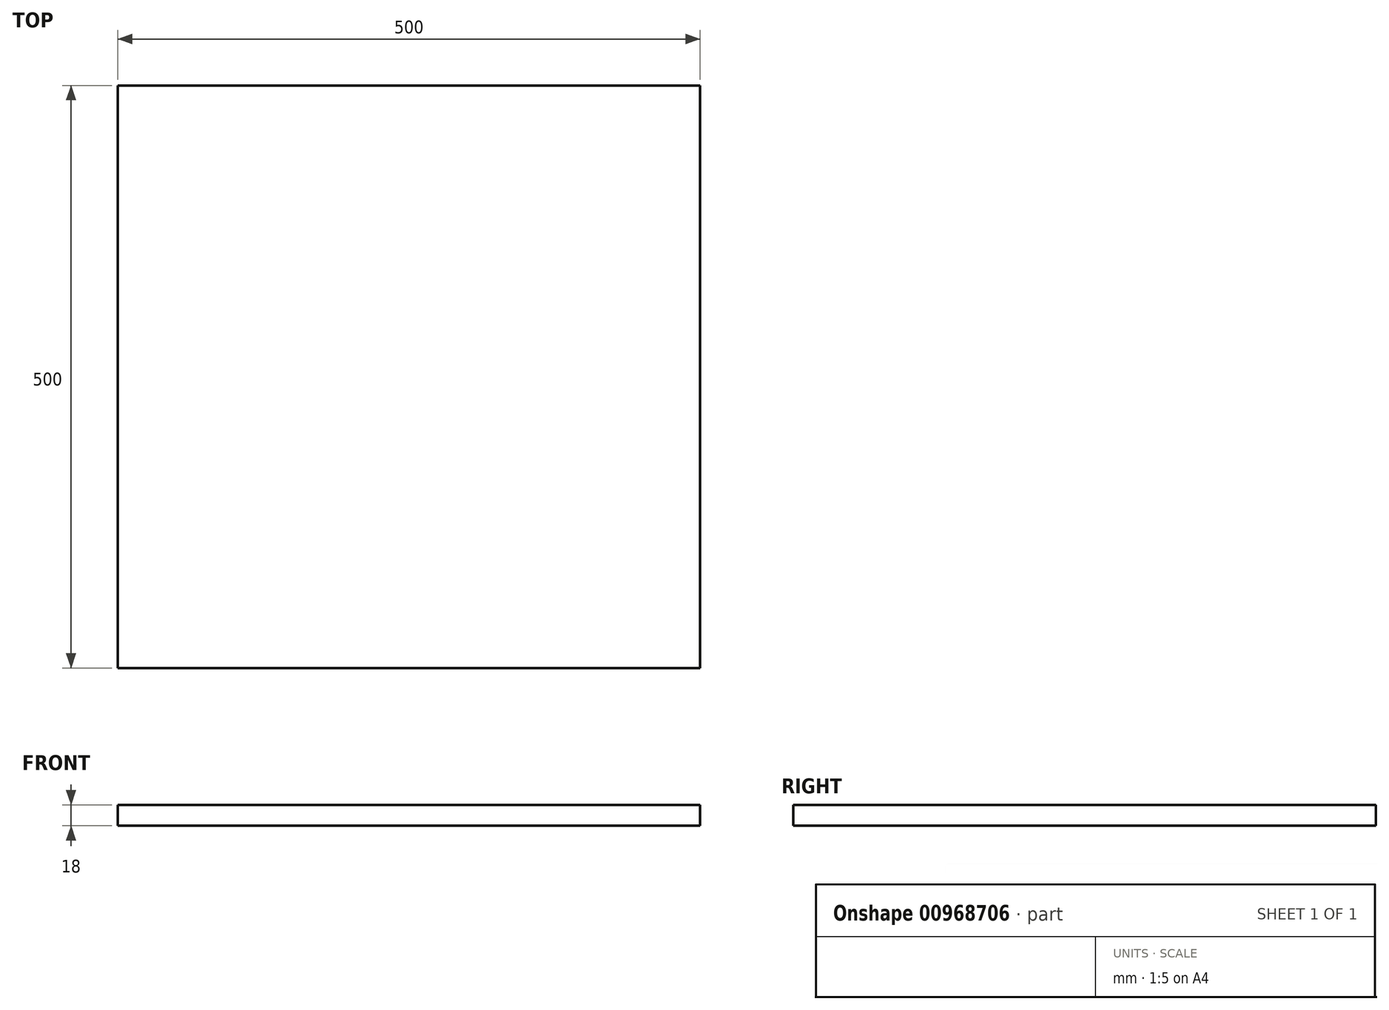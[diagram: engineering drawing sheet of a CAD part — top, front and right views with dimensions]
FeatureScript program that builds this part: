
annotation { "Feature Type Name" : "Feature", "Feature Type Description" : "" }
export const myFeature = defineFeature(function(context is Context, id is Id, definition is map)
    precondition{}
    {
        {
            var Q0;
            Q0=qCreatedBy(makeId("Top.planeOp"),FACE);
            var sketch = newSketch(context, id + "F0", { "sketchPlane" : qUnion([Q0])});
            skLineSegment(sketch, "E0.bottom", {"start": v(-84.69, -75.17) * mm, "end": v(415.31, -75.17) * mm});
            skLineSegment(sketch, "E0.top", {"start": v(-84.69, 424.83) * mm, "end": v(415.31, 424.83) * mm});
            skLineSegment(sketch, "E0.left", {"start": v(-84.69, -75.17) * mm, "end": v(-84.69, 424.83) * mm});
            skLineSegment(sketch, "E0.right", {"start": v(415.31, -75.17) * mm, "end": v(415.31, 424.83) * mm});
            skSolve(sketch);
        }
        {
            var Q0;
            Q0 = qSketchRegion(id + "F0", true);
            extrude(context, id + "F1", {"entities" : qUnion([Q0]), "depth" : 18 * mm, "offsetDistance" : 25 * mm});
        }
    });
